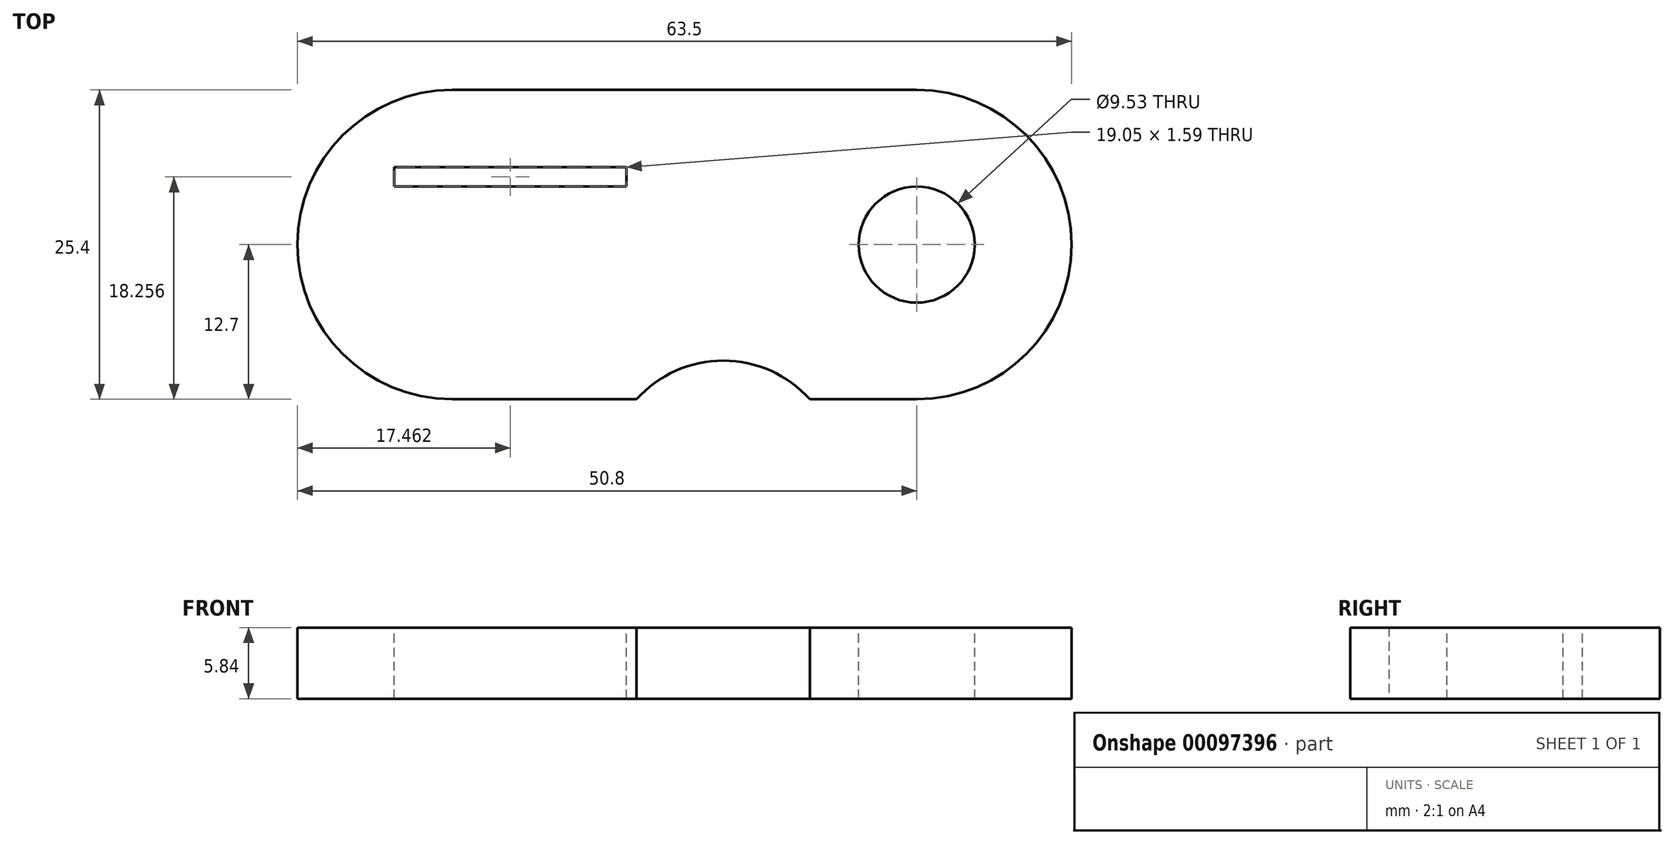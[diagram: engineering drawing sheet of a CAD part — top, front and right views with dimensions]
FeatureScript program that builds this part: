
annotation { "Feature Type Name" : "Feature", "Feature Type Description" : "" }
export const myFeature = defineFeature(function(context is Context, id is Id, definition is map)
    precondition{}
    {
        {
            var Q0;
            Q0=qCreatedBy(makeId("Top.planeOp"),FACE);
            var sketch = newSketch(context, id + "F0", { "sketchPlane" : qUnion([Q0])});
            skLineSegment(sketch, "E0.bottom", {"start": v(0, 0) * mm, "end": v(-38.1, 0) * mm});
            skLineSegment(sketch, "E0.top", {"start": v(0, 25.4) * mm, "end": v(-38.1, 25.4) * mm});
            skLineSegment(sketch, "E0.left", {"start": v(0, 0) * mm, "end": v(0, 25.4) * mm});
            skLineSegment(sketch, "E0.right", {"start": v(-38.1, 0) * mm, "end": v(-38.1, 25.4) * mm});
            skCircle(sketch, "E1", {"center": v(0, 12.7) * mm, "radius": 12.7 * mm});
            skCircle(sketch, "E2", {"center": v(-38.1, 12.7) * mm, "radius": 12.7 * mm});
            skSolve(sketch);
        }
        {
            var Q0;
            {var subQ0=sQuery(id+"F0.wireOp",EDGE,"E0.right");Q0=makeQuery(id+"F0.imprint","IMPRINT",FACE,{"disambiguationData":[TD([[makeQuery(id+"F0.imprint","IMPRINT",EDGE,{"derivedFrom":subQ0}),-1.0]])]});}
            var Q1;
            {var subQ0=sQuery(id+"F0.wireOp",EDGE,"E0.left");Q1=makeQuery(id+"F0.imprint","IMPRINT",FACE,{"disambiguationData":[TD([[makeQuery(id+"F0.imprint","IMPRINT",EDGE,{"derivedFrom":subQ0}),1.0]])]});}
            var Q2;
            {var subQ0=sQuery(id+"F0.wireOp",EDGE,"E0.bottom");Q2=makeQuery(id+"F0.imprint","IMPRINT",FACE,{"disambiguationData":[TD([[makeQuery(id+"F0.imprint","IMPRINT",EDGE,{"derivedFrom":subQ0}),-1.0]])]});}
            var Q3;
            {var subQ0=sQuery(id+"F0.wireOp",EDGE,"E0.top");Q3=makeQuery(id+"F0.imprint","IMPRINT",FACE,{"disambiguationData":[TD([[makeQuery(id+"F0.imprint","IMPRINT",EDGE,{"derivedFrom":subQ0}),1.0]])]});}
            var Q4;
            {var subQ0=sQuery(id+"F0.wireOp",EDGE,"E0.left");Q4=makeQuery(id+"F0.imprint","IMPRINT",FACE,{"disambiguationData":[TD([[makeQuery(id+"F0.imprint","IMPRINT",EDGE,{"derivedFrom":subQ0}),-1.0]])]});}
            var Q5;
            {var subQ0=sQuery(id+"F0.wireOp",EDGE,"E0.right");Q5=makeQuery(id+"F0.imprint","IMPRINT",FACE,{"disambiguationData":[TD([[makeQuery(id+"F0.imprint","IMPRINT",EDGE,{"derivedFrom":subQ0}),1.0]])]});}
            var Q6;
            {var subQ0=sQuery(id+"F0.wireOp",EDGE,"E2");var subQ1=sQuery(id+"F0.wireOp",EDGE,"E1");var subQ2=makeQuery(id+"F0.imprint","INTERSECT",VERTEX,{"disambiguationData":[OD(0.0)],"derivedFrom":[subQ1,subQ0]});Q6=makeQuery(id+"F0.imprint","IMPRINT",FACE,{"disambiguationData":[TD([[makeQuery(id+"F0.imprint","IMPRINT",EDGE,{"disambiguationData":[TD([[subQ2,-1.0]])],"derivedFrom":subQ1}),1.0]])]});}
            extrude(context, id + "F1", {"entities" : qUnion([Q0, Q1, Q2, Q3, Q4, Q5, Q6]), "depth" : 5.84 * mm});
        }
        {
            var Q0;
            Q0=makeQuery(id+"F1.opExtrude","CAP_FACE",FACE,{"disambiguationData":[OSD([sQuery(id+"F0.wireOp",EDGE,"E0.bottom"),sQuery(id+"F0.wireOp",EDGE,"E0.top"),sQuery(id+"F0.wireOp",EDGE,"E1"),sQuery(id+"F0.wireOp",EDGE,"E2")])],"isStart":false});
            var sketch = newSketch(context, id + "F2", { "sketchPlane" : qUnion([Q0])});
            skCircle(sketch, "E3", {"center": v(0, 12.7) * mm, "radius": 4.76 * mm});
            skSolve(sketch);
        }
        {
            var Q0;
            Q0=makeQuery(id+"F2.imprint","IMPRINT",FACE,{"disambiguationData":[TD([[makeQuery(id+"F2.imprint","IMPRINT",EDGE,{"derivedFrom":sQuery(id+"F2.wireOp",EDGE,"E3")}),1.0]])]});
            extrude(context, id + "F3", {"entities" : qUnion([Q0]), "operationType" : NewBodyOperationType.REMOVE, "oppositeDirection" : true, "depth" : 25.4 * mm});
        }
        {
            var Q0;
            Q0=makeQuery(id+"F1.opExtrude","CAP_FACE",FACE,{"disambiguationData":[OSD([sQuery(id+"F0.wireOp",EDGE,"E0.bottom"),sQuery(id+"F0.wireOp",EDGE,"E0.top"),sQuery(id+"F0.wireOp",EDGE,"E1"),sQuery(id+"F0.wireOp",EDGE,"E2")])],"isStart":false});
            var sketch = newSketch(context, id + "F4", { "sketchPlane" : qUnion([Q0])});
            skLineSegment(sketch, "E4.bottom", {"start": v(-42.86, 17.46) * mm, "end": v(-23.81, 17.46) * mm});
            skLineSegment(sketch, "E4.top", {"start": v(-42.86, 19.05) * mm, "end": v(-23.81, 19.05) * mm});
            skLineSegment(sketch, "E4.left", {"start": v(-42.86, 17.46) * mm, "end": v(-42.86, 19.05) * mm});
            skLineSegment(sketch, "E4.right", {"start": v(-23.81, 17.46) * mm, "end": v(-23.81, 19.05) * mm});
            skSolve(sketch);
        }
        {
            var Q0;
            Q0=makeQuery(id+"F4.imprint","IMPRINT",FACE,{"disambiguationData":[TD([[makeQuery(id+"F4.imprint","IMPRINT",EDGE,{"derivedFrom":sQuery(id+"F4.wireOp",EDGE,"E4.bottom")}),1.0]])]});
            extrude(context, id + "F5", {"entities" : qUnion([Q0]), "operationType" : NewBodyOperationType.REMOVE, "oppositeDirection" : true, "depth" : 25.4 * mm});
        }
        {
            var Q0;
            Q0=makeQuery(id+"F1.opExtrude","CAP_FACE",FACE,{"disambiguationData":[OSD([sQuery(id+"F0.wireOp",EDGE,"E0.bottom"),sQuery(id+"F0.wireOp",EDGE,"E0.top"),sQuery(id+"F0.wireOp",EDGE,"E1"),sQuery(id+"F0.wireOp",EDGE,"E2")])],"isStart":true});
            var sketch = newSketch(context, id + "F6", { "sketchPlane" : qUnion([Q0])});
            skCircle(sketch, "E5", {"center": v(-15.88, 6.35) * mm, "radius": 9.53 * mm});
            skPoint(sketch, "E6", {"position": v(-4.76, -12.7) * mm});
            skPoint(sketch, "E7", {"position": v(-6.35, 6.35) * mm});
            skPoint(sketch, "E8", {"position": v(-50.8, -12.7) * mm});
            skSolve(sketch);
        }
        {
            var Q0;
            {var subQ0=sQuery(id+"F6.wireOp",EDGE,"E5");var subQ1=makeQuery(id+"F1.opExtrude","CAP_EDGE",EDGE,{"disambiguationData":[OSD([sQuery(id+"F0.wireOp",EDGE,"E0.bottom")])],"isStart":true});var subQ2=makeQuery(id+"F6.imprint","INTERSECT",VERTEX,{"disambiguationData":[OD(0.0)],"derivedFrom":[subQ1,subQ0]});Q0=makeQuery(id+"F6.imprint","IMPRINT",FACE,{"disambiguationData":[TD([[makeQuery(id+"F6.imprint","IMPRINT",EDGE,{"disambiguationData":[TD([[subQ2,1.0]])],"derivedFrom":subQ0}),1.0]])]});}
            extrude(context, id + "F7", {"entities" : qUnion([Q0]), "operationType" : NewBodyOperationType.REMOVE, "oppositeDirection" : true, "depth" : 25.4 * mm});
        }
    });
